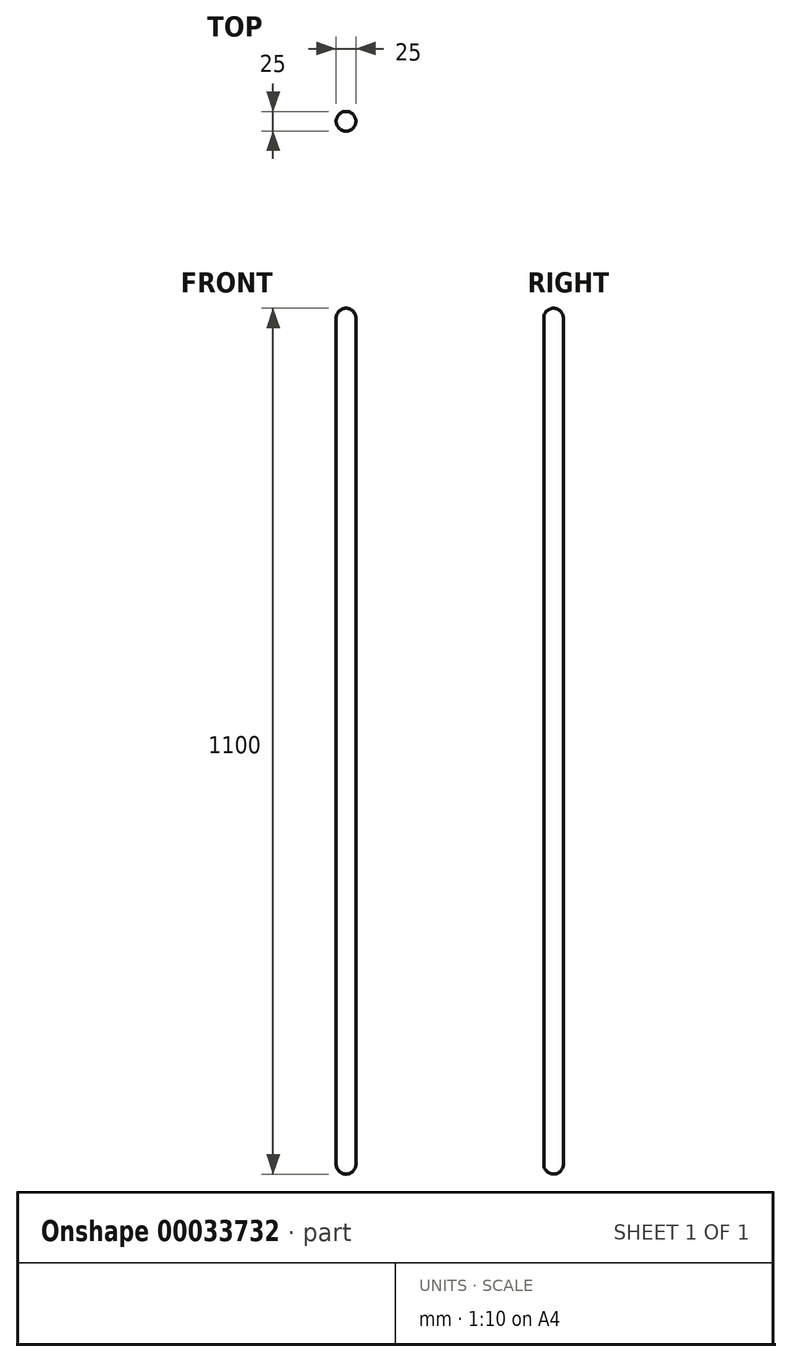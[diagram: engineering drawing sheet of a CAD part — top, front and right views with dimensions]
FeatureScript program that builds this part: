
annotation { "Feature Type Name" : "Feature", "Feature Type Description" : "" }
export const myFeature = defineFeature(function(context is Context, id is Id, definition is map)
    precondition{}
    {
        {
            var Q0;
            Q0=qCreatedBy(makeId("Front.planeOp"),FACE);
            var sketch = newSketch(context, id + "F0", { "sketchPlane" : qUnion([Q0])});
            skLineSegment(sketch, "E0.bottom", {"start": v(0, 550) * mm, "end": v(0, 550) * mm});
            skLineSegment(sketch, "E0.top", {"start": v(0, -550) * mm, "end": v(0, -550) * mm});
            skLineSegment(sketch, "E0.left", {"start": v(0, 550) * mm, "end": v(0, -550) * mm});
            skLineSegment(sketch, "E0.right", {"start": v(-12.5, 537.5) * mm, "end": v(-12.5, -537.5) * mm});
            skPoint(sketch, "E1.visualSharp", {"position": v(-12.5, 550) * mm});
            skArc(sketch, "E1.filletArc", {"start": v(0, 550) * mm, "mid": v(-8.84, 546.34) * mm, "end": v(-12.5, 537.5) * mm});
            skPoint(sketch, "E2.visualSharp", {"position": v(-12.5, -550) * mm});
            skArc(sketch, "E2.filletArc", {"start": v(-12.5, -537.5) * mm, "mid": v(-8.84, -546.34) * mm, "end": v(0, -550) * mm});
            skSolve(sketch);
        }
        {
            var Q0;
            Q0=makeQuery(id+"F0.imprint","IMPRINT",FACE,{"disambiguationData":[TD([[makeQuery(id+"F0.imprint","IMPRINT",EDGE,{"derivedFrom":sQuery(id+"F0.wireOp",EDGE,"E0.left")}),-1.0]])]});
            var Q1;
            Q1=sQuery(id+"F0.wireOp",EDGE,"E0.left");
            revolve(context, id + "F1", {"entities" : qUnion([Q0]), "axis" : qUnion([Q1]), "revolveType" : RevolveType.FULL});
        }
    });
